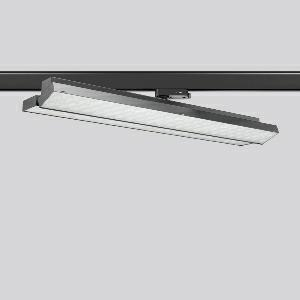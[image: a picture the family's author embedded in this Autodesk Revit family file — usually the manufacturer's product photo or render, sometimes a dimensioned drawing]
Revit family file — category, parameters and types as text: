
# Revit family: tx-move_742162_003_2_76_192c
name_source: partatom
category: Lighting Fixtures
units: mm (PartAtom-declared; Revit-internal decimal feet)

## family parameters
Cut with Voids When Loaded = No
Host = Face
Light Source = No
Part Type = Normal
Room Calculation Point = No
Round Connector Dimension = Use Diameter
Shared = No

## types (1)
- MultiLumen 1 (1 x LED Modul 927, 2100 lm, 2700)
    Apparent Load = 38 VA
    CIE Flux Codes = 77 96 99 100 100
    Color Rendering = 92
    Color Temperature = 2700
    Default Elevation = 1800 mm
    Description = Series: TX-MOVE
Multifunctional surface-mounted spotlight for area lighting. Very flat design. Housing: sheet steel, powder-coated. Rotation range: 356°. Swivel range: 90°. Consistent alignment possible with visible tilt scale. High-efficiency LED units with optimum light control thanks to clear plastic (PC) lens optics. Spezielle Mikrostrukturen reduzieren Gelbsaum. Symmetrical light distribution. Best colour rendering with CRI >90 for fresh products and coloured textiles. With adapter for RZB 3-circuit DALI tracks. Suitable for Track on ceiling. MultiLumen: Luminous flux adjustable in 3 steps. Factory setting is the highest luminous flux. Environmentally friendly and resource-saving due to replaceable and recyclable components. 
Colour: deep black, matt (RAL 9005)
Length: 570 mm
Width: 119 mm
Height: 88 mm
Lamp: LED
Socket: without socket
Colour temperature: 2700K
Colour rendering index (CRI): 90
System power: 38 W
Rated luminous flux: 4200 lm
Luminous efficiency: 111 lm/W
System power 2: 51 W
Rated luminous flux 2: 5500 lm
Luminous efficiency 2: 108 lm/W
System power 3: 62 W
Rated luminous flux 3: 6550 lm
Luminous efficiency 3: 106 lm/W
Control gear: Dimmable EVG, DALI
Protection class: I
Type of protection: IP 20
    Height = 75 mm
    Lamp = 1 x LED Modul 927
    Lamp Light Flux = 2100 lm
    Lamp count = 1
    Length = 569 mm
    Lifetime = 50000 h
    Luminous efficacy = 111 lm/W
    Manufacturer = RZB
    ModVariant = No
    Model = 742162.003.2.76
    Mounting Place = Ceiling
    Mounting Type = Surface mounted
    Number of Poles = 1
    OnlyDefault = Yes
    Power Factor = 1
    Product Name = TX-MOVE
    Product group = Track mounted projectors
    ProductGroupID = 301
    Protection Class = Protection class I
    Protection Degree = IP 20
    RLX_Detail_Level = 1
    RLX_Emergency_Light_Flux = 0 lm
    RLX_Emergency_Type = 0
    RLX_Emergency_Type_DB = No
    RlxData = <blob elided: 36953 chars, md5=03c3ec4b>
    Socket = socket
    Standby Power = 0 W
    System Light Flux = 4200 lm
    System Power = 38 W
    Type Comments = MultiLumen 1
    Type Image = 742162.003.jpg
    URL = http://relux.com
    VarID = multilumen_1
    Voltage = 0 V
    Weight = 0.00 kg
    Width = 119 mm

## geometry (parser evidence)
native form markers: Blend x4, Sweep x13
no freeform markers — native parametric forms only
